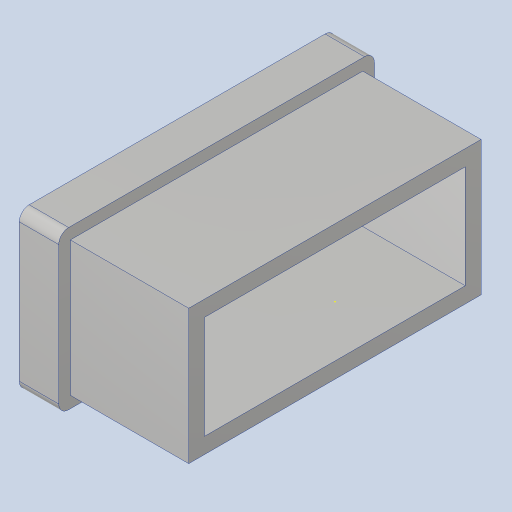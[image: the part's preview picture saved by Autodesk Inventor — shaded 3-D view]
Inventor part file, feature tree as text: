
AUTODESK INVENTOR PART (.ipt)
format: ipt  version: 2023.4 (Build 274418000, 418)  size: 294,912 bytes
history: native  units: in
note: dims shown in document units (in); Inventor stores cm internally (conversion verified against a paired STEP export)
features: sketch x4, extrude x2, shell x1, fillet x1, emboss x1
ambient origin geometry x8: Origin, YZ Plane, XZ Plane, XY Plane, X Axis, Y Axis, Z Axis, Center Point
bodies: Solid1 (feature_tree)
feature tree (9):
  extrude  "Extrusion1"  Depth=1.0in
  extrude  "Extrusion2"  Depth=0.0078in
  shell  "Shell1"  Thickness=0.25in
  fillet  "Fillet1"  Radius=0.0625in
  emboss  "Emboss1"
  sketch  "Sketch4"  dims[d10=0.011in d11=0.75in d12=0.0in d13=0.1in d14=0.0625in d15=0.25in d16=0.0in]
  sketch  "Sketch1"  dims[d0=2.0in d1=1.0in]
  sketch  "Sketch2"  dims[d4=0.0625in d5=0.0078in d6=0.25in d7=0.0in d8=0.0625in]
  sketch  "Sketch3"  dims[d9=0.0625in]
